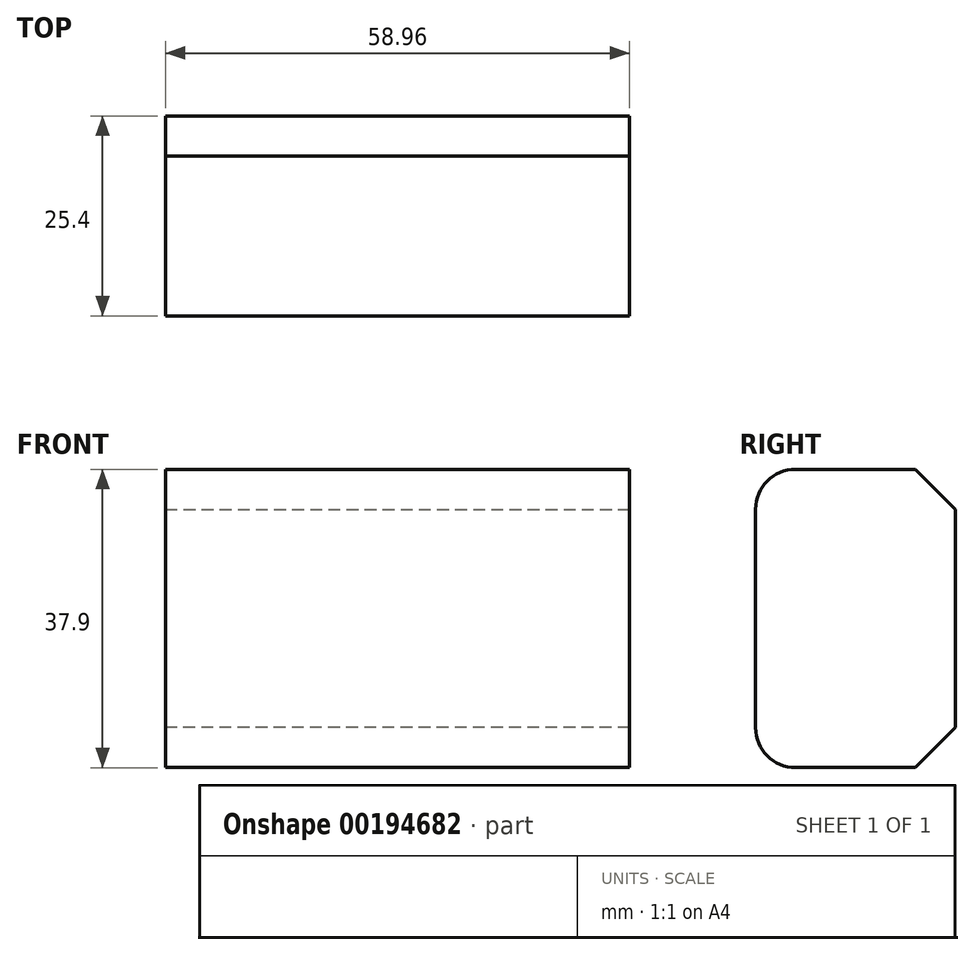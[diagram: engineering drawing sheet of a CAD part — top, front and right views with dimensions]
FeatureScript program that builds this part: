
annotation { "Feature Type Name" : "Feature", "Feature Type Description" : "" }
export const myFeature = defineFeature(function(context is Context, id is Id, definition is map)
    precondition{}
    {
        {
            var Q0;
            Q0=qCreatedBy(makeId("Front.planeOp"),FACE);
            var sketch = newSketch(context, id + "F0", { "sketchPlane" : qUnion([Q0])});
            skLineSegment(sketch, "E0.bottom", {"start": v(29.48, 18.95) * mm, "end": v(-29.48, 18.95) * mm});
            skLineSegment(sketch, "E0.top", {"start": v(29.48, -18.95) * mm, "end": v(-29.48, -18.95) * mm});
            skLineSegment(sketch, "E0.left", {"start": v(29.48, 18.95) * mm, "end": v(29.48, -18.95) * mm});
            skLineSegment(sketch, "E0.right", {"start": v(-29.48, 18.95) * mm, "end": v(-29.48, -18.95) * mm});
            skPoint(sketch, "E0.middle", {"position": v(0, 0) * mm});
            skSolve(sketch);
        }
        {
            var Q0;
            Q0=makeQuery(id+"F0.imprint","IMPRINT",FACE,{"disambiguationData":[TD([[makeQuery(id+"F0.imprint","IMPRINT",EDGE,{"derivedFrom":sQuery(id+"F0.wireOp",EDGE,"E0.bottom")}),1.0]])]});
            extrude(context, id + "F1", {"entities" : qUnion([Q0]), "depth" : 25.4 * mm});
        }
        {
            var Q0;
            Q0=makeQuery(id+"F1.opExtrude","CAP_EDGE",EDGE,{"disambiguationData":[OSD([sQuery(id+"F0.wireOp",EDGE,"E0.bottom")])],"isStart":false});
            var Q1;
            Q1=makeQuery(id+"F1.opExtrude","CAP_EDGE",EDGE,{"disambiguationData":[OSD([sQuery(id+"F0.wireOp",EDGE,"E0.top")])],"isStart":false});
            fillet(context, id + "F2", {"entities" : qUnion([Q0, Q1]), "radius" : 5.08 * mm, "tangentPropagation" : true, "allowEdgeOverflow" : false});
        }
        {
            var Q0;
            Q0=makeQuery(id+"F1.opExtrude","CAP_EDGE",EDGE,{"disambiguationData":[OSD([sQuery(id+"F0.wireOp",EDGE,"E0.top")])],"isStart":true});
            var Q1;
            Q1=makeQuery(id+"F1.opExtrude","CAP_EDGE",EDGE,{"disambiguationData":[OSD([sQuery(id+"F0.wireOp",EDGE,"E0.bottom")])],"isStart":true});
            chamfer(context, id + "F3", {"entities" : qUnion([Q0, Q1]), "width" : 5.08 * mm, "tangentPropagation" : true});
        }
    });
